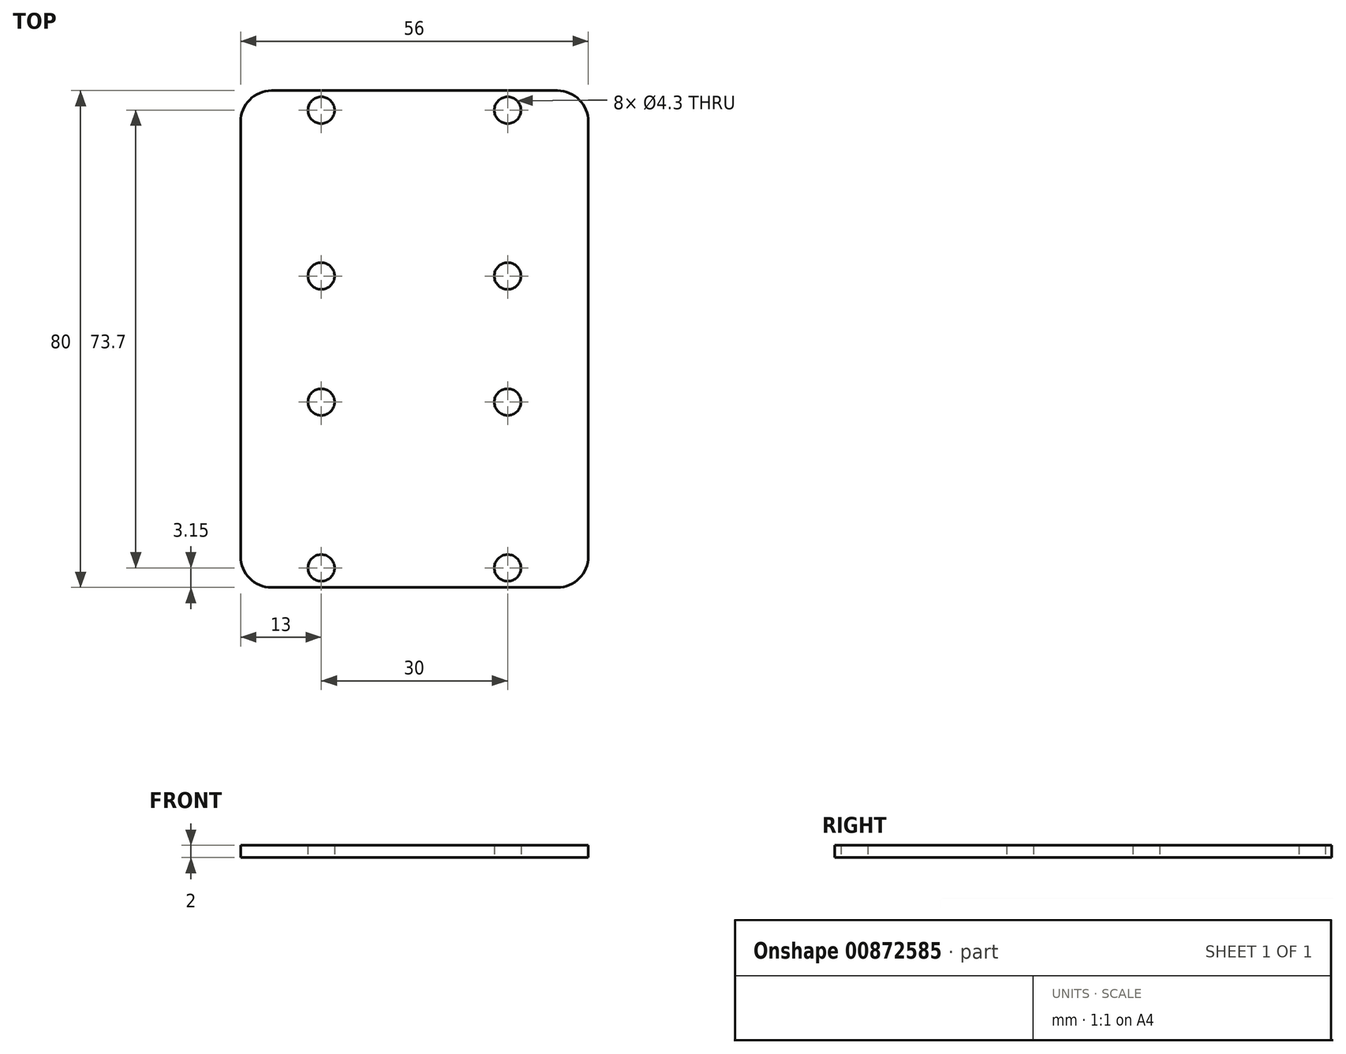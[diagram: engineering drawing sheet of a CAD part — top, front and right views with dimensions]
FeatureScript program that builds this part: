
annotation { "Feature Type Name" : "Feature", "Feature Type Description" : "" }
export const myFeature = defineFeature(function(context is Context, id is Id, definition is map)
    precondition{}
    {
        {
            var Q0;
            Q0=qCreatedBy(makeId("Top.planeOp"),FACE);
            var sketch = newSketch(context, id + "F0", { "sketchPlane" : qUnion([Q0])});
            skLineSegment(sketch, "E0.bottom", {"start": v(23, 40) * mm, "end": v(-23, 40) * mm});
            skLineSegment(sketch, "E0.top", {"start": v(23, -40) * mm, "end": v(-23, -40) * mm});
            skLineSegment(sketch, "E0.left", {"start": v(28, 35) * mm, "end": v(28, -35) * mm});
            skLineSegment(sketch, "E0.right", {"start": v(-28, 35) * mm, "end": v(-28, -35) * mm});
            skPoint(sketch, "E0.middle", {"position": v(0, 0) * mm});
            skLineSegment(sketch, "E1", {"start": v(-28, -40) * mm, "end": v(-4, -40) * mm, "construction": true});
            skLineSegment(sketch, "E2", {"start": v(-28, -40) * mm, "end": v(-15, -40) * mm, "construction": true});
            skLineSegment(sketch, "E3", {"start": v(-15, -40) * mm, "end": v(-15, -7) * mm, "construction": true});
            skLineSegment(sketch, "E4", {"start": v(-15, -23.5) * mm, "end": v(-15, -17.5) * mm});
            skLineSegment(sketch, "E5", {"start": v(-15, -23.5) * mm, "end": v(-15, -10.15) * mm, "construction": true});
            skCircle(sketch, "E6", {"center": v(-15, -10.15) * mm, "radius": 2.15 * mm});
            skLineSegment(sketch, "E7", {"start": v(-15, -23.5) * mm, "end": v(-28, -23.5) * mm, "construction": true});
            skCircle(sketch, "E8.MirrorC", {"center": v(-15, -36.85) * mm, "radius": 2.15 * mm});
            skCircle(sketch, "E9.MirrorC", {"center": v(-15, 36.85) * mm, "radius": 2.15 * mm});
            skCircle(sketch, "E10.MirrorC", {"center": v(-15, 10.15) * mm, "radius": 2.15 * mm});
            skCircle(sketch, "E11.MirrorC", {"center": v(15, 36.85) * mm, "radius": 2.15 * mm});
            skCircle(sketch, "E12.MirrorC", {"center": v(15, 10.15) * mm, "radius": 2.15 * mm});
            skCircle(sketch, "E13.MirrorC", {"center": v(15, -36.85) * mm, "radius": 2.15 * mm});
            skCircle(sketch, "E14.MirrorC", {"center": v(15, -10.15) * mm, "radius": 2.15 * mm});
            skPoint(sketch, "E15.visualSharp", {"position": v(-28, 40) * mm});
            skArc(sketch, "E15.filletArc", {"start": v(-23, 40) * mm, "mid": v(-26.54, 38.54) * mm, "end": v(-28, 35) * mm});
            skPoint(sketch, "E16.visualSharp", {"position": v(-28, -40) * mm});
            skArc(sketch, "E16.filletArc", {"start": v(-28, -35) * mm, "mid": v(-26.54, -38.54) * mm, "end": v(-23, -40) * mm});
            skPoint(sketch, "E17.visualSharp", {"position": v(28, -40) * mm});
            skArc(sketch, "E17.filletArc", {"start": v(23, -40) * mm, "mid": v(26.54, -38.54) * mm, "end": v(28, -35) * mm});
            skPoint(sketch, "E18.visualSharp", {"position": v(28, 40) * mm});
            skArc(sketch, "E18.filletArc", {"start": v(28, 35) * mm, "mid": v(26.54, 38.54) * mm, "end": v(23, 40) * mm});
            skLineSegment(sketch, "E19", {"start": v(-4, -40) * mm, "end": v(2, -40) * mm, "construction": true});
            skLineSegment(sketch, "E20", {"start": v(2, -40) * mm, "end": v(2, -23.5) * mm, "construction": true});
            skLineSegment(sketch, "E21", {"start": v(-15, -39) * mm, "end": v(-15, -40) * mm, "construction": true});
            skSolve(sketch);
        }
        {
            var Q0;
            Q0=makeQuery(id+"F0.imprint","IMPRINT",FACE,{"disambiguationData":[TD([[makeQuery(id+"F0.imprint","IMPRINT",EDGE,{"derivedFrom":sQuery(id+"F0.wireOp",EDGE,"E0.bottom")}),1.0]])]});
            extrude(context, id + "F1", {"entities" : qUnion([Q0]), "depth" : 2 * mm, "offsetDistance" : 25 * mm});
        }
    });
